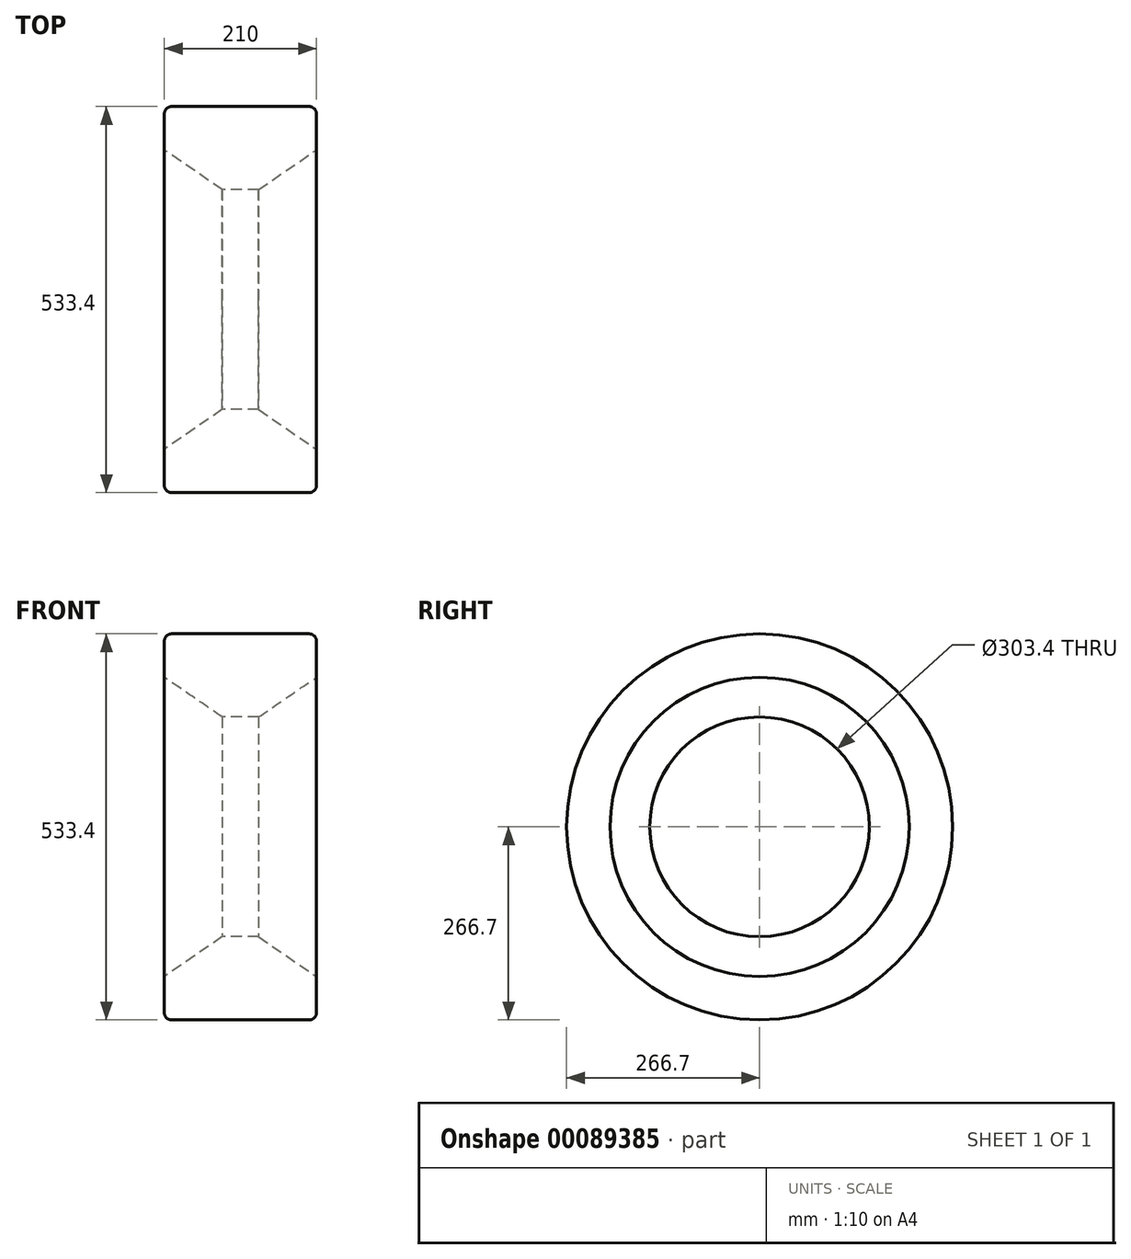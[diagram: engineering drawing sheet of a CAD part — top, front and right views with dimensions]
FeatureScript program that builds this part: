
annotation { "Feature Type Name" : "Feature", "Feature Type Description" : "" }
export const myFeature = defineFeature(function(context is Context, id is Id, definition is map)
    precondition{}
    {
        {
            var Q0;
            Q0=qCreatedBy(makeId("Front.planeOp"),FACE);
            var sketch = newSketch(context, id + "F0", { "sketchPlane" : qUnion([Q0])});
            skLineSegment(sketch, "E0", {"start": v(-105, 266.7) * mm, "end": v(105, 266.7) * mm});
            skLineSegment(sketch, "E1", {"start": v(105, 266.7) * mm, "end": v(105, 206.7) * mm});
            skLineSegment(sketch, "E2", {"start": v(105, 206.7) * mm, "end": v(25, 151.7) * mm});
            skLineSegment(sketch, "E3", {"start": v(25, 151.7) * mm, "end": v(-25, 151.7) * mm});
            skLineSegment(sketch, "E4", {"start": v(-25, 151.7) * mm, "end": v(-105, 206.7) * mm});
            skLineSegment(sketch, "E5", {"start": v(-105, 206.7) * mm, "end": v(-105, 266.7) * mm});
            skLineSegment(sketch, "E6", {"start": v(-225.37, 0) * mm, "end": v(191.42, 0) * mm, "construction": true});
            skSolve(sketch);
        }
        {
            var Q0;
            Q0=makeQuery(id+"F0.imprint","IMPRINT",FACE,{"disambiguationData":[TD([[makeQuery(id+"F0.imprint","IMPRINT",EDGE,{"derivedFrom":sQuery(id+"F0.wireOp",EDGE,"E0")}),-1.0]])]});
            var Q1;
            Q1=sQuery(id+"F0.wireOp",EDGE,"E6");
            revolve(context, id + "F1", {"entities" : qUnion([Q0]), "axis" : qUnion([Q1]), "revolveType" : RevolveType.FULL});
        }
        {
            var Q0;
            Q0=makeQuery(id+"F1.opRevolve","SWEPT_EDGE",EDGE,{"disambiguationData":[OSD([sQuery(id+"F0.wireOp",EDGE,"E0"),sQuery(id+"F0.wireOp",EDGE,"E1")])]});
            var Q1;
            Q1=makeQuery(id+"F1.opRevolve","SWEPT_EDGE",EDGE,{"disambiguationData":[OSD([sQuery(id+"F0.wireOp",EDGE,"E0"),sQuery(id+"F0.wireOp",EDGE,"E5")])]});
            fillet(context, id + "F2", {"entities" : qUnion([Q0, Q1]), "radius" : 10 * mm, "tangentPropagation" : true, "allowEdgeOverflow" : false});
        }
    });
